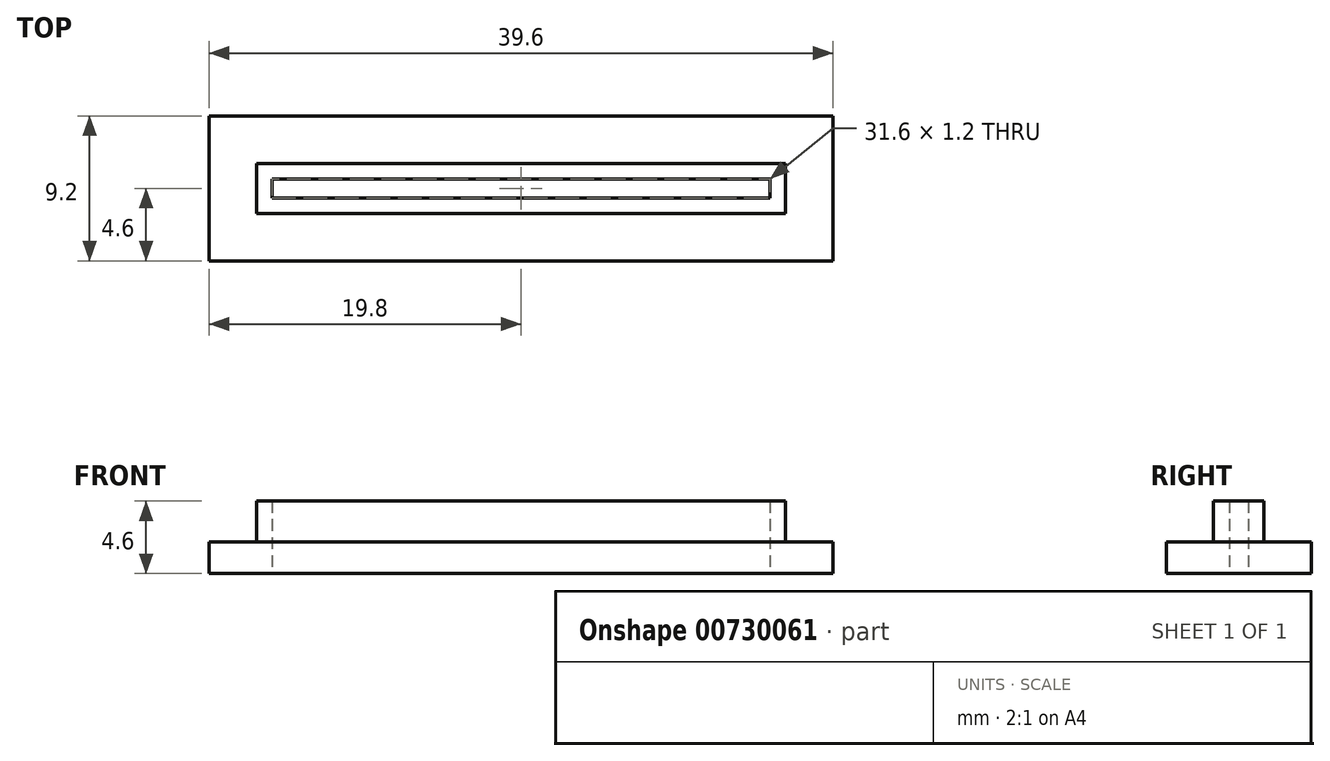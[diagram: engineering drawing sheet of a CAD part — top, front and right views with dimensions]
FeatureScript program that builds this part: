
annotation { "Feature Type Name" : "Feature", "Feature Type Description" : "" }
export const myFeature = defineFeature(function(context is Context, id is Id, definition is map)
    precondition{}
    {
        {
            var Q0;
            Q0=qCreatedBy(makeId("Top.planeOp"),FACE);
            var sketch = newSketch(context, id + "F0", { "sketchPlane" : qUnion([Q0])});
            skLineSegment(sketch, "E0.bottom", {"start": v(-15.3, 5.2) * mm, "end": v(24.3, 5.2) * mm});
            skLineSegment(sketch, "E0.top", {"start": v(-15.3, -4) * mm, "end": v(24.3, -4) * mm});
            skLineSegment(sketch, "E0.left", {"start": v(-15.3, 5.2) * mm, "end": v(-15.3, -4) * mm});
            skLineSegment(sketch, "E0.right", {"start": v(24.3, 5.2) * mm, "end": v(24.3, -4) * mm});
            skLineSegment(sketch, "E1.bottom", {"start": v(-11.3, 1.2) * mm, "end": v(20.3, 1.2) * mm});
            skLineSegment(sketch, "E1.top", {"start": v(-11.3, 0) * mm, "end": v(20.3, 0) * mm});
            skLineSegment(sketch, "E1.left", {"start": v(-11.3, 1.2) * mm, "end": v(-11.3, 0) * mm});
            skLineSegment(sketch, "E1.right", {"start": v(20.3, 1.2) * mm, "end": v(20.3, 0) * mm});
            skSolve(sketch);
        }
        {
            var Q0;
            Q0=makeQuery(id+"F0.imprint","IMPRINT",FACE,{"disambiguationData":[TD([[makeQuery(id+"F0.imprint","IMPRINT",EDGE,{"derivedFrom":sQuery(id+"F0.wireOp",EDGE,"E0.bottom")}),-1.0]])]});
            extrude(context, id + "F1", {"entities" : qUnion([Q0]), "depth" : 2 * mm, "offsetDistance" : 25 * mm});
        }
        {
            var Q0;
            Q0=makeQuery(id+"F1.opExtrude","CAP_FACE",FACE,{"disambiguationData":[OSD([sQuery(id+"F0.wireOp",EDGE,"E0.bottom"),sQuery(id+"F0.wireOp",EDGE,"E0.top"),sQuery(id+"F0.wireOp",EDGE,"E0.left"),sQuery(id+"F0.wireOp",EDGE,"E0.right"),sQuery(id+"F0.wireOp",EDGE,"E1.bottom"),sQuery(id+"F0.wireOp",EDGE,"E1.top"),sQuery(id+"F0.wireOp",EDGE,"E1.left"),sQuery(id+"F0.wireOp",EDGE,"E1.right")])],"isStart":false});
            var sketch = newSketch(context, id + "F2", { "sketchPlane" : qUnion([Q0])});
            skLineSegment(sketch, "E2.bottom", {"start": v(-12.3, -1) * mm, "end": v(21.3, -1) * mm});
            skLineSegment(sketch, "E2.top", {"start": v(-12.3, 2.2) * mm, "end": v(21.3, 2.2) * mm});
            skLineSegment(sketch, "E2.left", {"start": v(-12.3, -1) * mm, "end": v(-12.3, 2.2) * mm});
            skLineSegment(sketch, "E2.right", {"start": v(21.3, -1) * mm, "end": v(21.3, 2.2) * mm});
            skSolve(sketch);
        }
        {
            var Q0;
            Q0=makeQuery(id+"F2.imprint","IMPRINT",FACE,{"disambiguationData":[TD([[makeQuery(id+"F2.imprint","IMPRINT",EDGE,{"derivedFrom":sQuery(id+"F2.wireOp",EDGE,"E2.bottom")}),1.0]])]});
            extrude(context, id + "F3", {"entities" : qUnion([Q0]), "operationType" : NewBodyOperationType.ADD, "depth" : 2.6 * mm, "offsetDistance" : 25 * mm});
        }
    });
